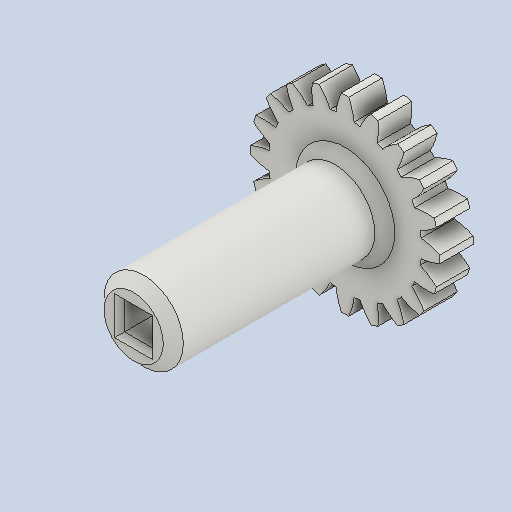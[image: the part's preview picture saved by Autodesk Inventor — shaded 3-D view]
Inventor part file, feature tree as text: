
AUTODESK INVENTOR PART (.ipt)
format: ipt  version: 2022 (Build 260153000, 153)  size: 294,912 bytes
history: native  units: in
note: dims shown in document units (in); Inventor stores cm internally (conversion verified against a paired STEP export)
features: other x12, sketch x4, plane x3
ambient origin geometry x8: Origin, YZ Plane, XZ Plane, XY Plane, X Axis, Y Axis, Z Axis, Center Point
bodies: Solid1 (feature_tree)
feature tree (19):
  other  "Spur Gear23_MIR.ipt"
  other  "Solid1::Spur Gear23_MIR.ipt"
  other  "TaggingFeature1"
  sketch  "Sketch1"  dims[d0=0.3937in]
  sketch  "Sketch2"  dims[d9=0.0in d14=0.0in d15=1.0in d16=0.0in d17=0.0in d18=0.0in d19=1.0in]
  sketch  "Sketch3"
  sketch  "Sketch4"
  plane  "XZ Plane_1"
  plane  "Work Plane2"
  plane  "Work Plane3"
  other  "Srf1"
  other  "Srf1::Derived"
  other  "Start plane iMate"
  other  "Distance iMate"
  other  "Position iMate"
  other  "Mesh iMate"
  other  "Axis iMate"
  other  "Mesh iMate2"
  other  "Align iMate"
